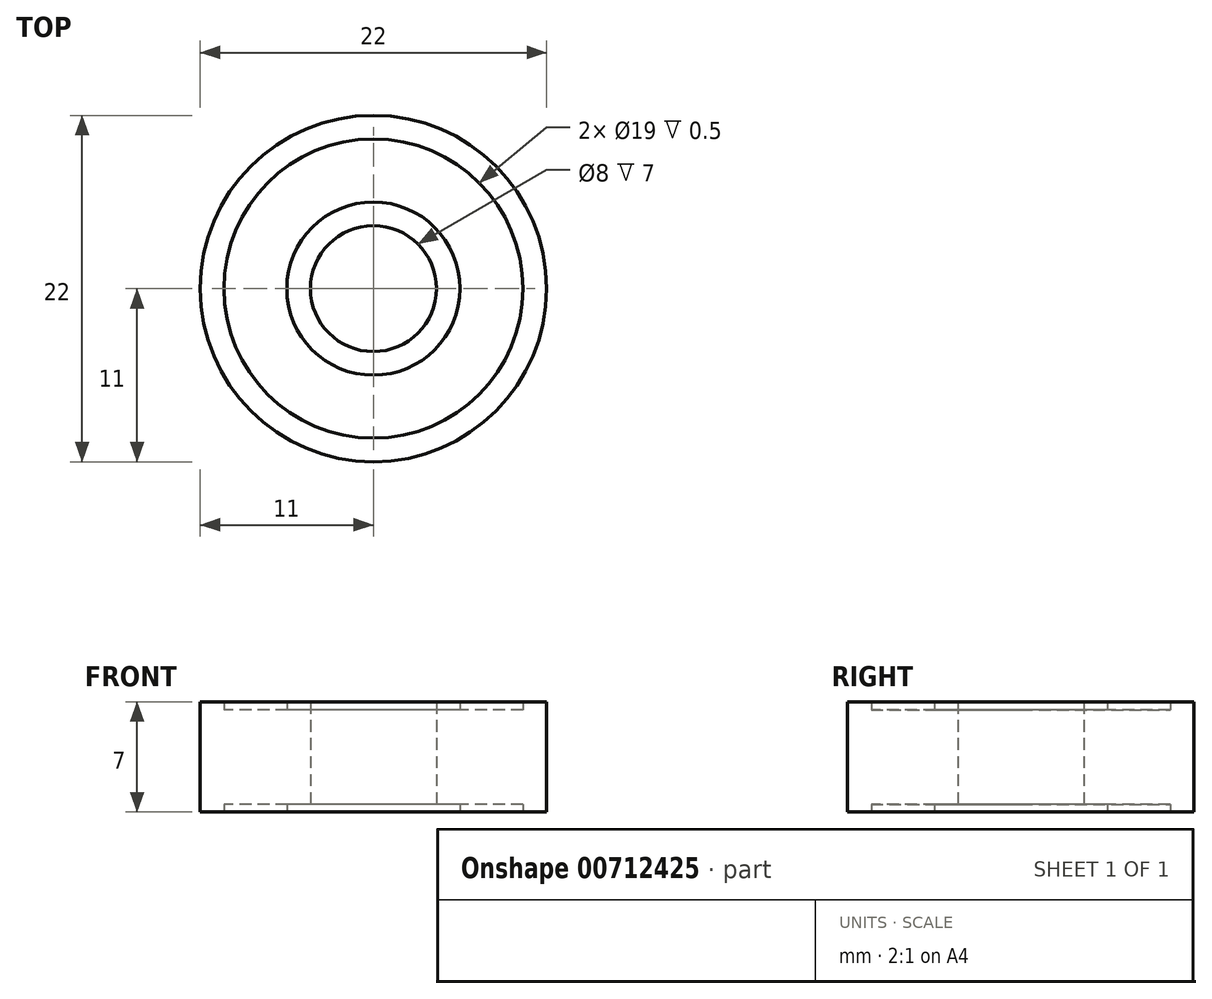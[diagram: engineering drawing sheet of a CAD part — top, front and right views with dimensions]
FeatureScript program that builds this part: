
annotation { "Feature Type Name" : "Feature", "Feature Type Description" : "" }
export const myFeature = defineFeature(function(context is Context, id is Id, definition is map)
    precondition{}
    {
        {
            var Q0;
            Q0=qCreatedBy(makeId("Top.planeOp"),FACE);
            var sketch = newSketch(context, id + "F0", { "sketchPlane" : qUnion([Q0])});
            skCircle(sketch, "E0", {"center": v(0, 0) * mm, "radius": 11 * mm});
            skCircle(sketch, "E1", {"center": v(0, 0) * mm, "radius": 4 * mm});
            skCircle(sketch, "E2.0", {"center": v(0, 0) * mm, "radius": 9.5 * mm});
            skCircle(sketch, "E3.0", {"center": v(0, 0) * mm, "radius": 5.5 * mm});
            skSolve(sketch);
        }
        {
            var Q0;
            Q0=makeQuery(id+"F0.imprint","IMPRINT",FACE,{"disambiguationData":[TD([[makeQuery(id+"F0.imprint","IMPRINT",EDGE,{"derivedFrom":sQuery(id+"F0.wireOp",EDGE,"E0")}),1.0]])]});
            var Q1;
            Q1=makeQuery(id+"F0.imprint","IMPRINT",FACE,{"disambiguationData":[TD([[makeQuery(id+"F0.imprint","IMPRINT",EDGE,{"derivedFrom":sQuery(id+"F0.wireOp",EDGE,"E1")}),-1.0]])]});
            extrude(context, id + "F1", {"entities" : qUnion([Q0, Q1]), "depth" : 7 * mm, "offsetDistance" : 25 * mm, "symmetric" : true});
        }
        {
            var Q0;
            Q0=makeQuery(id+"F0.imprint","IMPRINT",FACE,{"disambiguationData":[TD([[makeQuery(id+"F0.imprint","IMPRINT",EDGE,{"derivedFrom":sQuery(id+"F0.wireOp",EDGE,"E2.0")}),1.0]])]});
            extrude(context, id + "F2", {"entities" : qUnion([Q0]), "operationType" : NewBodyOperationType.ADD, "depth" : 6 * mm, "offsetDistance" : 25 * mm, "symmetric" : true});
        }
    });
